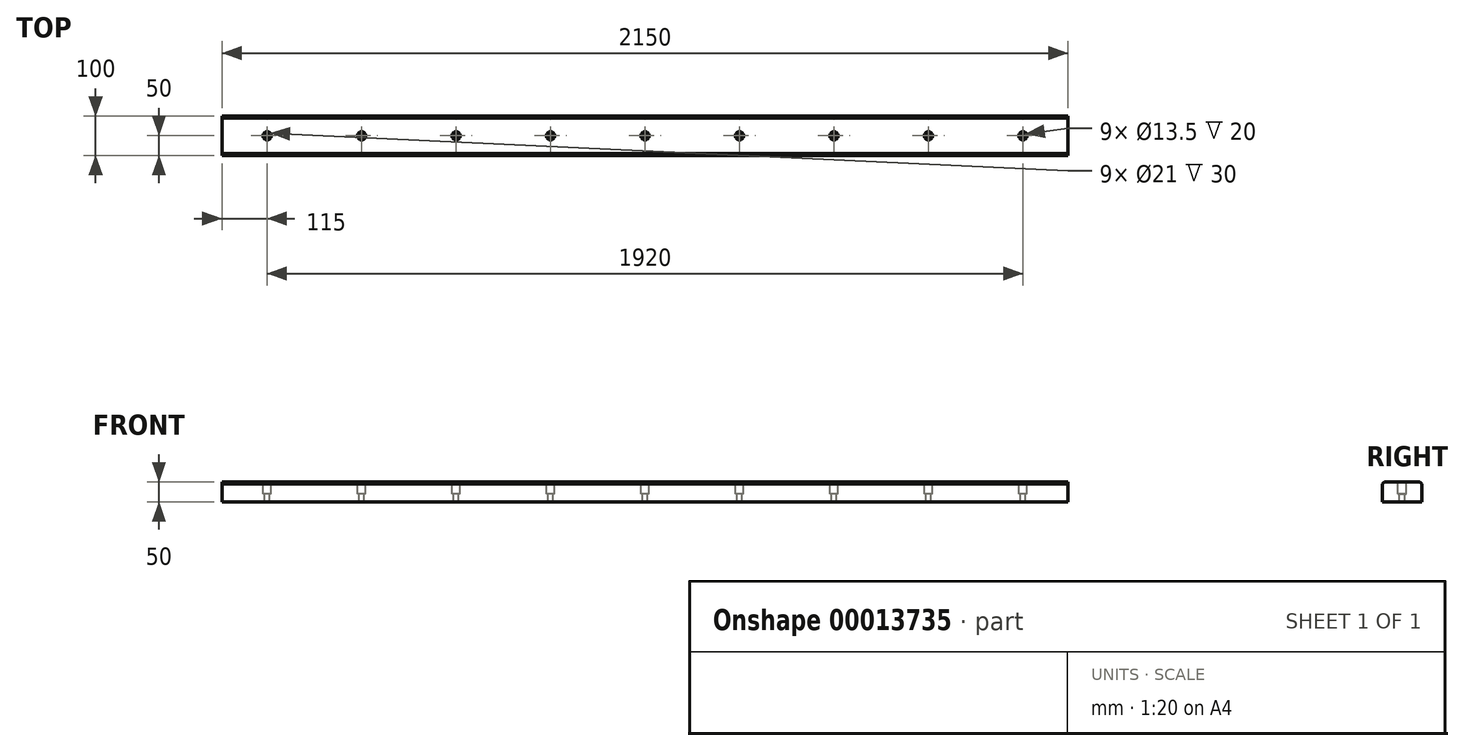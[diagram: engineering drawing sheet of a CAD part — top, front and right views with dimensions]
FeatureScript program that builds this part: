
annotation { "Feature Type Name" : "Feature", "Feature Type Description" : "" }
export const myFeature = defineFeature(function(context is Context, id is Id, definition is map)
    precondition{}
    {
        {
            var Q0;
            Q0=qCreatedBy(makeId("Right.planeOp"),FACE);
            var sketch = newSketch(context, id + "F0", { "sketchPlane" : qUnion([Q0])});
            skLineSegment(sketch, "E0", {"start": v(0, 0) * mm, "end": v(0, 50.61) * mm, "construction": true});
            skLineSegment(sketch, "E1", {"start": v(0, 0) * mm, "end": v(-81.02, 0) * mm, "construction": true});
            skLineSegment(sketch, "E2.0", {"start": v(-50, 0) * mm, "end": v(-50, 25) * mm, "construction": true});
            skLineSegment(sketch, "E3.0", {"start": v(0, 25) * mm, "end": v(-81.02, 25) * mm, "construction": true});
            skLineSegment(sketch, "E4.0.MirrorCS", {"start": v(0, -25) * mm, "end": v(-81.02, -25) * mm, "construction": true});
            skLineSegment(sketch, "E5.0.MirrorCS", {"start": v(50, -25) * mm, "end": v(50, 25) * mm, "construction": true});
            skPoint(sketch, "E6.orphan", {"position": v(50, 0) * mm});
            skLineSegment(sketch, "E7.bottom", {"start": v(-50, 25) * mm, "end": v(50, 25) * mm});
            skLineSegment(sketch, "E7.top", {"start": v(-50, -25) * mm, "end": v(50, -25) * mm});
            skLineSegment(sketch, "E7.left", {"start": v(-50, 25) * mm, "end": v(-50, -25) * mm});
            skLineSegment(sketch, "E7.right", {"start": v(50, 25) * mm, "end": v(50, -25) * mm});
            skSolve(sketch);
        }
        {
            var Q0;
            Q0 = qSketchRegion(id + "F0", true);
            extrude(context, id + "F1", {"entities" : qUnion([Q0]), "endBound" : BoundingType.SYMMETRIC, "depth" : 2150 * mm});
        }
        {
            var Q0;
            Q0=makeQuery(id+"F1.opExtrude","SWEPT_EDGE",EDGE,{"disambiguationData":[OSD([sQuery(id+"F0.wireOp",EDGE,"E7.bottom"),sQuery(id+"F0.wireOp",EDGE,"E7.left")])]});
            var Q1;
            Q1=makeQuery(id+"F1.opExtrude","SWEPT_EDGE",EDGE,{"disambiguationData":[OSD([sQuery(id+"F0.wireOp",EDGE,"E7.bottom"),sQuery(id+"F0.wireOp",EDGE,"E7.right")])]});
            chamfer(context, id + "F2", {"entities" : qUnion([Q0, Q1]), "width" : 5 * mm, "tangentPropagation" : true});
        }
        {
            var Q0;
            Q0=makeQuery(id+"F1.opExtrude","SWEPT_FACE",FACE,{"disambiguationData":[OSD([sQuery(id+"F0.wireOp",EDGE,"E7.bottom")])]});
            var sketch = newSketch(context, id + "F3", { "sketchPlane" : qUnion([Q0])});
            skLineSegment(sketch, "E8", {"start": v(-1075, 0) * mm, "end": v(1075, 0) * mm, "construction": true});
            skLineSegment(sketch, "E9", {"start": v(0, 0) * mm, "end": v(0, -201.23) * mm, "construction": true});
            skLineSegment(sketch, "E10.1.0.0", {"start": v(-240, 0) * mm, "end": v(-240, -201.23) * mm, "construction": true});
            skLineSegment(sketch, "E10.2.0.0", {"start": v(-480, 0) * mm, "end": v(-480, -201.23) * mm, "construction": true});
            skLineSegment(sketch, "E10.3.0.0", {"start": v(-720, 0) * mm, "end": v(-720, -201.23) * mm, "construction": true});
            skLineSegment(sketch, "E10.4.0.0", {"start": v(-960, 0) * mm, "end": v(-960, -201.23) * mm, "construction": true});
            skLineSegment(sketch, "E10.direction1", {"start": v(0, -201.23) * mm, "end": v(-240, -201.23) * mm, "construction": true});
            skCircle(sketch, "E11", {"center": v(-960, 0) * mm, "radius": 6.75 * mm});
            skCircle(sketch, "E12.1.0.0", {"center": v(-720, 0) * mm, "radius": 6.75 * mm});
            skCircle(sketch, "E12.2.0.0", {"center": v(-480, 0) * mm, "radius": 6.75 * mm});
            skLineSegment(sketch, "E12.direction1", {"start": v(-960, 0) * mm, "end": v(-720, 0) * mm, "construction": true});
            skCircle(sketch, "E13.0.3.0", {"center": v(-240, 0) * mm, "radius": 6.75 * mm});
            skCircle(sketch, "E13.0.4.0", {"center": v(0, 0) * mm, "radius": 6.75 * mm});
            skCircle(sketch, "E13.0.5.0", {"center": v(240, 0) * mm, "radius": 6.75 * mm});
            skCircle(sketch, "E13.0.6.0", {"center": v(480, 0) * mm, "radius": 6.75 * mm});
            skCircle(sketch, "E13.0.7.0", {"center": v(720, 0) * mm, "radius": 6.75 * mm});
            skCircle(sketch, "E13.0.8.0", {"center": v(960, 0) * mm, "radius": 6.75 * mm});
            skSolve(sketch);
        }
        {
            var Q0;
            Q0=sQuery(id+"F3.wireOp",VERTEX,"E10.4.0.0.start");
            var Q1;
            Q1=sQuery(id+"F3.wireOp",VERTEX,"E12.1.0.0.center");
            var Q2;
            Q2=sQuery(id+"F3.wireOp",VERTEX,"E12.2.0.0.center");
            var Q3;
            Q3=sQuery(id+"F3.wireOp",VERTEX,"E10.1.0.0.start");
            var Q4;
            Q4=sQuery(id+"F3.wireOp",VERTEX,"E9.start");
            var Q5;
            Q5=sQuery(id+"F3.wireOp",VERTEX,"E13.0.5.0.center");
            var Q6;
            Q6=sQuery(id+"F3.wireOp",VERTEX,"E13.0.6.0.center");
            var Q7;
            Q7=sQuery(id+"F3.wireOp",VERTEX,"E13.0.7.0.center");
            var Q8;
            Q8=sQuery(id+"F3.wireOp",VERTEX,"E13.0.8.0.center");
            var Q9;
            Q9=makeQuery(id+"F1.opExtrude","SWEPT_BODY",BODY,{"disambiguationData":[OSD([sQuery(id+"F0.wireOp",EDGE,"E7.bottom"),sQuery(id+"F0.wireOp",EDGE,"E7.top"),sQuery(id+"F0.wireOp",EDGE,"E7.left"),sQuery(id+"F0.wireOp",EDGE,"E7.right")])]});
            hole(context, id + "F4", {"style" : HoleStyle.C_BORE, "holeDiameter" : 13.5 * mm, "cBoreDiameter" : 21 * mm, "cBoreDepth" : 30 * mm, "endStyle" : HoleEndStyle.THROUGH, "locations" : qUnion([Q0, Q1, Q2, Q3, Q4, Q5, Q6, Q7, Q8]), "scope" : qUnion([Q9])});
        }
    });
